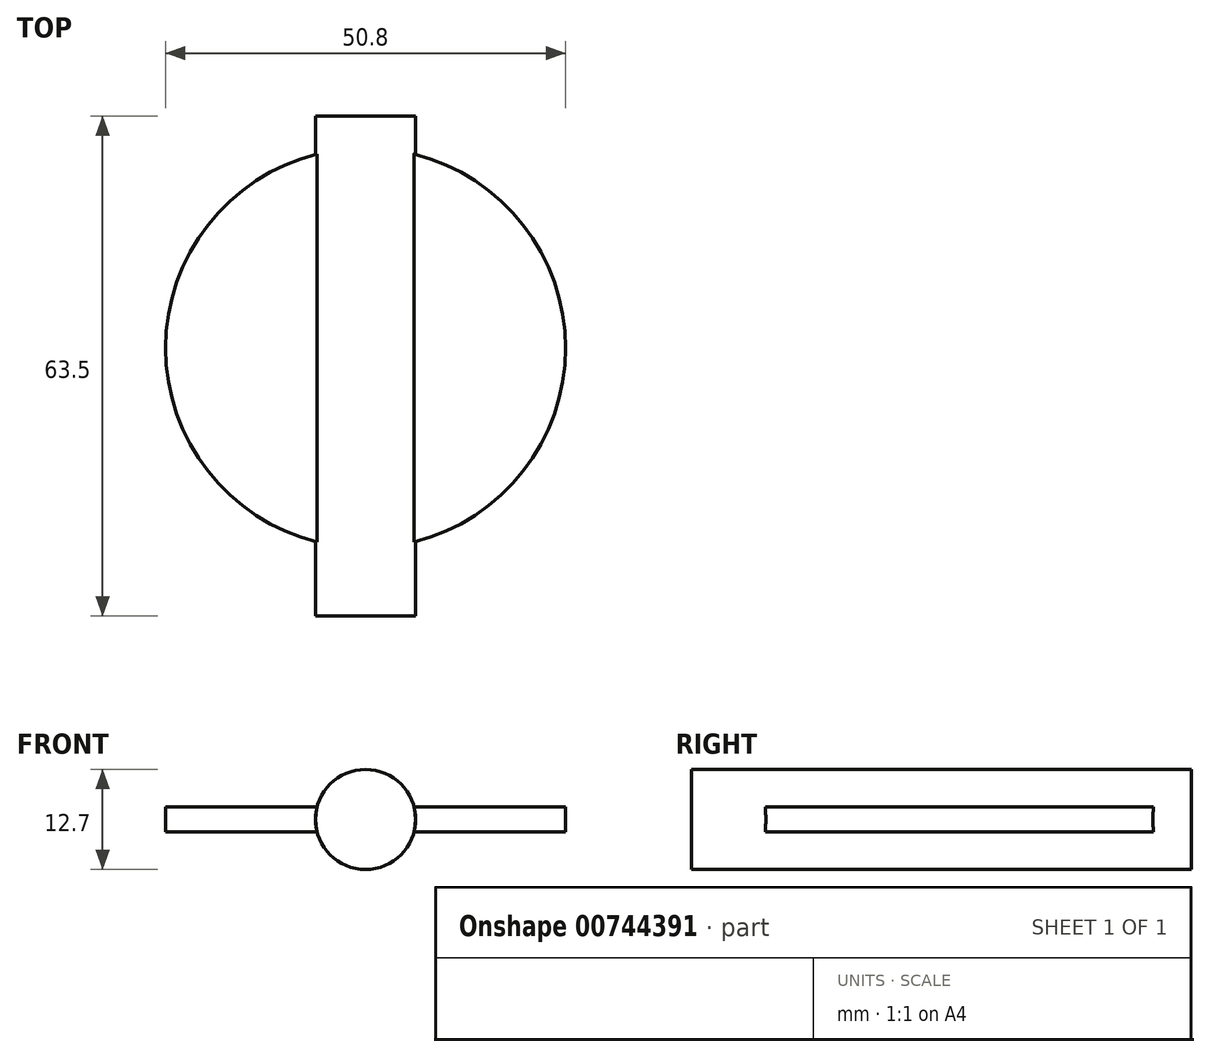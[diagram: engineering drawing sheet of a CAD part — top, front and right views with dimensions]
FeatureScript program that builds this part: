
annotation { "Feature Type Name" : "Feature", "Feature Type Description" : "" }
export const myFeature = defineFeature(function(context is Context, id is Id, definition is map)
    precondition{}
    {
        {
            var Q0;
            Q0=qCreatedBy(makeId("Front.planeOp"),FACE);
            var sketch = newSketch(context, id + "F0", { "sketchPlane" : qUnion([Q0])});
            skCircle(sketch, "E0", {"center": v(0, 0) * mm, "radius": 6.35 * mm});
            skSolve(sketch);
        }
        {
            var Q0;
            Q0=qSketchRegion(id+"F0",true);
            extrude(context, id + "F1", {"entities" : qUnion([Q0]), "depth" : 63.5 * mm});
        }
        {
            var Q0;
            Q0=qCreatedBy(makeId("Top.planeOp"),FACE);
            var sketch = newSketch(context, id + "F2", { "sketchPlane" : qUnion([Q0])});
            skCircle(sketch, "E1", {"center": v(0, -29.47) * mm, "radius": 25.4 * mm});
            skSolve(sketch);
        }
        {
            var Q0;
            Q0=makeQuery(id+"F2.imprint","IMPRINT",FACE,{"disambiguationData":[TD([[makeQuery(id+"F2.imprint","IMPRINT",EDGE,{"derivedFrom":sQuery(id+"F2.wireOp",EDGE,"E1")}),1.0]])]});
            extrude(context, id + "F3", {"entities" : qUnion([Q0]), "operationType" : NewBodyOperationType.ADD, "endBound" : BoundingType.SYMMETRIC, "depth" : 3.17 * mm});
        }
    });
